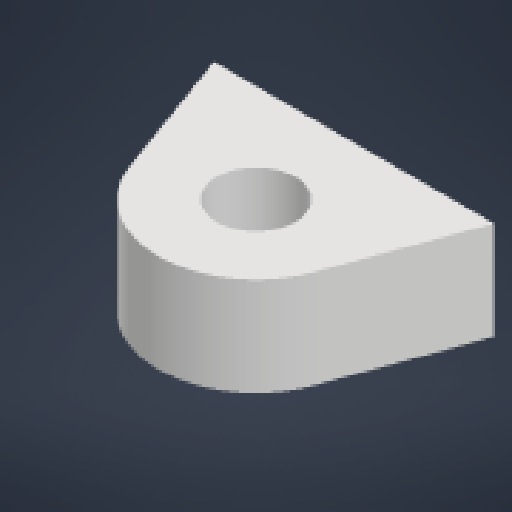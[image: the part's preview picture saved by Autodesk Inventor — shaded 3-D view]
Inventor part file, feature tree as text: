
AUTODESK INVENTOR PART (.ipt)
format: ipt  version: 2024 (Build 280153000, 153)  size: 213,504 bytes
history: native  units: mm
features: reference x6, other x5, extrude x4, sketch x4, fillet x1
ambient origin geometry x8: Origin, YZ Plane, XZ Plane, XY Plane, X Axis, Y Axis, Z Axis, Center Point
bodies: Body1 (feature_tree)
feature tree (20):
  other  "Твердое тело1"
  extrude  "Выдавливание1"  Depth=14.28148mm
  extrude  "Выдавливание2"  Depth=14.28148mm
  extrude  "Выдавливание3"  Depth=6.710101mm
  extrude  "Выдавливание4"  Depth=6.710101mm
  fillet  "Сопряжение1"  Radius=12.217305mm
  sketch  "Эскиз1"
  reference  "Ссылка1"
  reference  "Ссылка2"
  sketch  "Эскиз2"
  sketch  "Эскиз3"
  reference  "Ссылка3"
  sketch  "Эскиз4"
  reference  "Ссылка4"
  reference  "Ссылка5"
  reference  "Ссылка6"
  parser-record x1  (decoder bookkeeping rows leaked as tree rows — omitted from the tree; the rows remain in map.json)
  other  "cum_holder_asembly.iam"
  other  "cum_holder_down:1"
  other  "cum:1"
note: 1 file-system path scrubbed to <path> (originals preserved in map.json)
